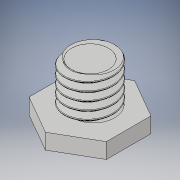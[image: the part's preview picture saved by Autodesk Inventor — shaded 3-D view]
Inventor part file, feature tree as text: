
AUTODESK INVENTOR PART (.ipt)
format: ipt  version: 2019 (Build 230136000, 136)  size: 544,768 bytes
history: native  units: in
note: dims shown in document units (in); Inventor stores cm internally (conversion verified against a paired STEP export)
features: sketch x5, extrude x2, revolve x2, thread x1, helix x1
ambient origin geometry x8: Origin, YZ Plane, XZ Plane, XY Plane, X Axis, Y Axis, Z Axis, Center Point
bodies: Solid1 (feature_tree), Solid3 (feature_tree)
feature tree (11):
  extrude  "Extrusion1"  Depth=0.315in TaperAngle=0.0deg
  extrude  "Extrusion2"  Depth=0.3937in TaperAngle=0.0deg
  thread  "Thread1"  [1 undecoded]
  revolve  "Revolution3"  [1 undecoded]
  revolve  "Revolution4"  [1 undecoded]
  helix  "Coil3"  [1 undecoded]
  sketch  "Sketch1"  dims[d0=0.375in d1=0.315in d2=0.0in]
  sketch  "Sketch2"  dims[d3=0.5906in d4=0.1181in d5=0.0in d16=0.3937in d17=0.0in]
  sketch  "Sketch7"  dims[d25=0.3779in d37=0.3779in d38=0.01in d39=0.01in]
  sketch  "Sketch8"  dims[d42=0.0625in d44=0.3779in d46=0.0in]
  sketch  "Sketch9"  dims[d47=0.0in d48=0.0626in d49=0.44in d50=0.3937in d51=0.0in d52=0.0in d53=0.0in d54=0.0in d55=0.0in]
note: 4 required parameter values undecoded (feature->parameter linkage not recoverable at this tier; creation-order binding heuristic only, values carry confidence <= 0.55)